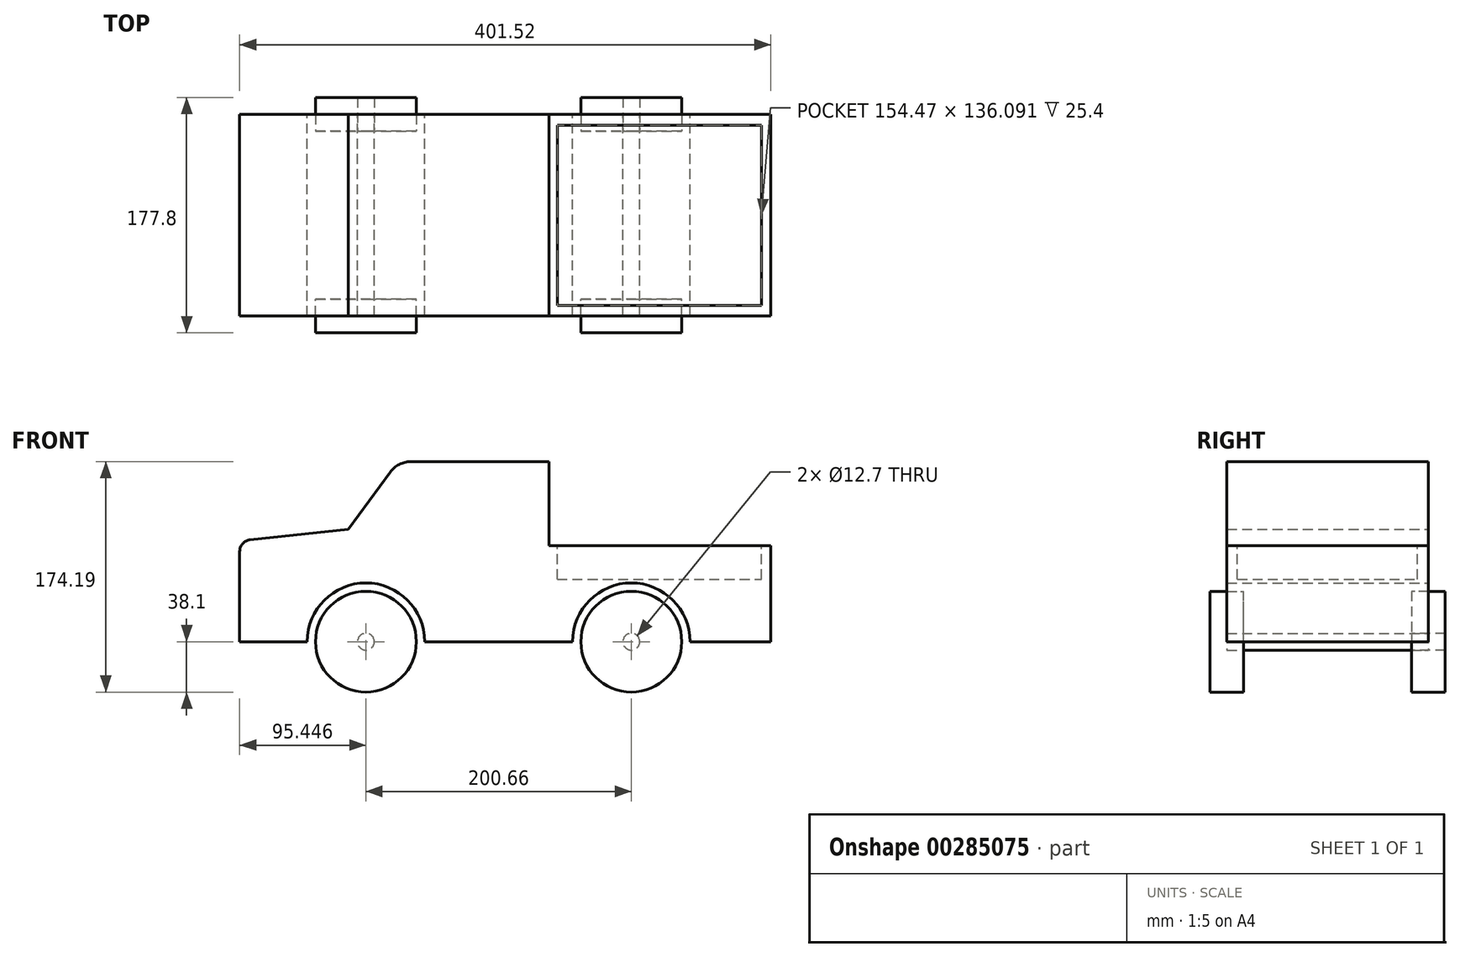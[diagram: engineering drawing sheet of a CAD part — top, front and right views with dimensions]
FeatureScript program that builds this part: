
annotation { "Feature Type Name" : "Feature", "Feature Type Description" : "" }
export const myFeature = defineFeature(function(context is Context, id is Id, definition is map)
    precondition{}
    {
        {
            var Q0;
            Q0=qCreatedBy(makeId("Front.planeOp"),FACE);
            var sketch = newSketch(context, id + "F0", { "sketchPlane" : qUnion([Q0])});
            skLineSegment(sketch, "E0", {"start": v(0, 0) * mm, "end": v(0, 68.2) * mm});
            skLineSegment(sketch, "E1", {"start": v(7.96, 77.04) * mm, "end": v(82.1, 84.83) * mm});
            skArc(sketch, "E2", {"start": v(139.9, 0) * mm, "mid": v(95.45, 44.45) * mm, "end": v(51, 0) * mm});
            skLineSegment(sketch, "E3", {"start": v(139.9, 0) * mm, "end": v(251.66, 0) * mm});
            skArc(sketch, "E4", {"start": v(340.56, 0) * mm, "mid": v(296.1, 44.45) * mm, "end": v(251.66, 0) * mm});
            skLineSegment(sketch, "E5", {"start": v(82.1, 84.83) * mm, "end": v(113.87, 128.28) * mm});
            skLineSegment(sketch, "E6", {"start": v(129.25, 136.09) * mm, "end": v(233.88, 136.09) * mm});
            skLineSegment(sketch, "E7", {"start": v(233.88, 136.09) * mm, "end": v(233.88, 72.59) * mm});
            skLineSegment(sketch, "E8", {"start": v(233.88, 72.59) * mm, "end": v(401.52, 72.59) * mm});
            skLineSegment(sketch, "E9", {"start": v(401.52, 72.59) * mm, "end": v(401.52, 0) * mm});
            skLineSegment(sketch, "E10", {"start": v(340.56, 0) * mm, "end": v(401.52, 0) * mm});
            skLineSegment(sketch, "E11", {"start": v(0, 0) * mm, "end": v(51, 0) * mm});
            skPoint(sketch, "E12.visualSharp", {"position": v(119.58, 136.09) * mm});
            skArc(sketch, "E12.filletArc", {"start": v(129.25, 136.09) * mm, "mid": v(120.62, 134.03) * mm, "end": v(113.87, 128.28) * mm});
            skPoint(sketch, "E13.visualSharp", {"position": v(0, 76.2) * mm});
            skArc(sketch, "E13.filletArc", {"start": v(7.96, 77.04) * mm, "mid": v(2.28, 74.14) * mm, "end": v(0, 68.2) * mm});
            skSolve(sketch);
        }
        {
            var Q0;
            Q0=makeQuery(id+"F0.imprint","IMPRINT",FACE,{"disambiguationData":[TD([[makeQuery(id+"F0.imprint","IMPRINT",EDGE,{"derivedFrom":sQuery(id+"F0.wireOp",EDGE,"E0")}),-1.0]])]});
            extrude(context, id + "F1", {"entities" : qUnion([Q0]), "depth" : 152.4 * mm});
        }
        {
            var Q0;
            Q0=makeQuery(id+"F1.opExtrude","CAP_FACE",FACE,{"disambiguationData":[OSD([sQuery(id+"F0.wireOp",EDGE,"E0"),sQuery(id+"F0.wireOp",EDGE,"E1"),sQuery(id+"F0.wireOp",EDGE,"E2"),sQuery(id+"F0.wireOp",EDGE,"E3"),sQuery(id+"F0.wireOp",EDGE,"E4"),sQuery(id+"F0.wireOp",EDGE,"E5"),sQuery(id+"F0.wireOp",EDGE,"E6"),sQuery(id+"F0.wireOp",EDGE,"E7"),sQuery(id+"F0.wireOp",EDGE,"E8"),sQuery(id+"F0.wireOp",EDGE,"E9"),sQuery(id+"F0.wireOp",EDGE,"E10"),sQuery(id+"F0.wireOp",EDGE,"E11")])],"isStart":false});
            var sketch = newSketch(context, id + "F2", { "sketchPlane" : qUnion([Q0])});
            skCircle(sketch, "E14", {"center": v(95.45, 0) * mm, "radius": 38.1 * mm});
            skCircle(sketch, "E15", {"center": v(296.1, 0) * mm, "radius": 38.1 * mm});
            skSolve(sketch);
        }
        {
            var Q0;
            Q0=makeQuery(id+"F2.imprint","IMPRINT",FACE,{"disambiguationData":[TD([[makeQuery(id+"F2.imprint","IMPRINT",EDGE,{"derivedFrom":sQuery(id+"F2.wireOp",EDGE,"E14")}),1.0]])]});
            var Q1;
            Q1=makeQuery(id+"F2.imprint","IMPRINT",FACE,{"disambiguationData":[TD([[makeQuery(id+"F2.imprint","IMPRINT",EDGE,{"derivedFrom":sQuery(id+"F2.wireOp",EDGE,"E15")}),1.0]])]});
            extrude(context, id + "F3", {"entities" : qUnion([Q0, Q1]), "endBound" : BoundingType.SYMMETRIC, "depth" : 25.4 * mm});
        }
        {
            var Q0;
            Q0=makeQuery(id+"F1.opExtrude","CAP_FACE",FACE,{"disambiguationData":[OSD([sQuery(id+"F0.wireOp",EDGE,"E0"),sQuery(id+"F0.wireOp",EDGE,"E1"),sQuery(id+"F0.wireOp",EDGE,"E2"),sQuery(id+"F0.wireOp",EDGE,"E3"),sQuery(id+"F0.wireOp",EDGE,"E4"),sQuery(id+"F0.wireOp",EDGE,"E5"),sQuery(id+"F0.wireOp",EDGE,"E6"),sQuery(id+"F0.wireOp",EDGE,"E7"),sQuery(id+"F0.wireOp",EDGE,"E8"),sQuery(id+"F0.wireOp",EDGE,"E9"),sQuery(id+"F0.wireOp",EDGE,"E10"),sQuery(id+"F0.wireOp",EDGE,"E11")])],"isStart":true});
            var sketch = newSketch(context, id + "F4", { "sketchPlane" : qUnion([Q0])});
            skCircle(sketch, "E16", {"center": v(-296.1, 0) * mm, "radius": 38.1 * mm});
            skCircle(sketch, "E17", {"center": v(-95.45, 0) * mm, "radius": 38.1 * mm});
            skCircle(sketch, "E18", {"center": v(-296.1, 0) * mm, "radius": 6.35 * mm});
            skCircle(sketch, "E19", {"center": v(-95.45, 0) * mm, "radius": 6.35 * mm});
            skSolve(sketch);
        }
        {
            var Q0;
            Q0=makeQuery(id+"F4.imprint","IMPRINT",FACE,{"disambiguationData":[TD([[makeQuery(id+"F4.imprint","IMPRINT",EDGE,{"derivedFrom":sQuery(id+"F4.wireOp",EDGE,"E18")}),1.0]])]});
            var Q1;
            Q1=makeQuery(id+"F4.imprint","IMPRINT",FACE,{"disambiguationData":[TD([[makeQuery(id+"F4.imprint","IMPRINT",EDGE,{"derivedFrom":sQuery(id+"F4.wireOp",EDGE,"E19")}),1.0]])]});
            extrude(context, id + "F5", {"entities" : qUnion([Q0, Q1]), "oppositeDirection" : true, "depth" : 152.4 * mm});
        }
        {
            var Q0;
            Q0=makeQuery(id+"F4.imprint","IMPRINT",FACE,{"disambiguationData":[TD([[makeQuery(id+"F4.imprint","IMPRINT",EDGE,{"derivedFrom":sQuery(id+"F4.wireOp",EDGE,"E16")}),1.0]])]});
            var Q1;
            Q1=makeQuery(id+"F4.imprint","IMPRINT",FACE,{"disambiguationData":[TD([[makeQuery(id+"F4.imprint","IMPRINT",EDGE,{"derivedFrom":sQuery(id+"F4.wireOp",EDGE,"E17")}),1.0]])]});
            extrude(context, id + "F6", {"entities" : qUnion([Q0, Q1]), "endBound" : BoundingType.SYMMETRIC, "depth" : 25.4 * mm});
        }
        {
            var Q0;
            Q0=makeQuery(id+"F1.opExtrude","SWEPT_FACE",FACE,{"disambiguationData":[OSD([sQuery(id+"F0.wireOp",EDGE,"E8")])]});
            var sketch = newSketch(context, id + "F7", { "sketchPlane" : qUnion([Q0])});
            skLineSegment(sketch, "E20.bottom", {"start": v(240.11, -144.44) * mm, "end": v(394.58, -144.44) * mm});
            skLineSegment(sketch, "E20.top", {"start": v(240.11, -8.35) * mm, "end": v(394.58, -8.35) * mm});
            skLineSegment(sketch, "E20.left", {"start": v(240.11, -144.44) * mm, "end": v(240.11, -8.35) * mm});
            skLineSegment(sketch, "E20.right", {"start": v(394.58, -144.44) * mm, "end": v(394.58, -8.35) * mm});
            skSolve(sketch);
        }
        {
            var Q0;
            Q0 = qSketchRegion(id + "F7", true);
            extrude(context, id + "F8", {"entities" : qUnion([Q0]), "operationType" : NewBodyOperationType.REMOVE, "oppositeDirection" : true, "depth" : 25.4 * mm});
        }
    });
